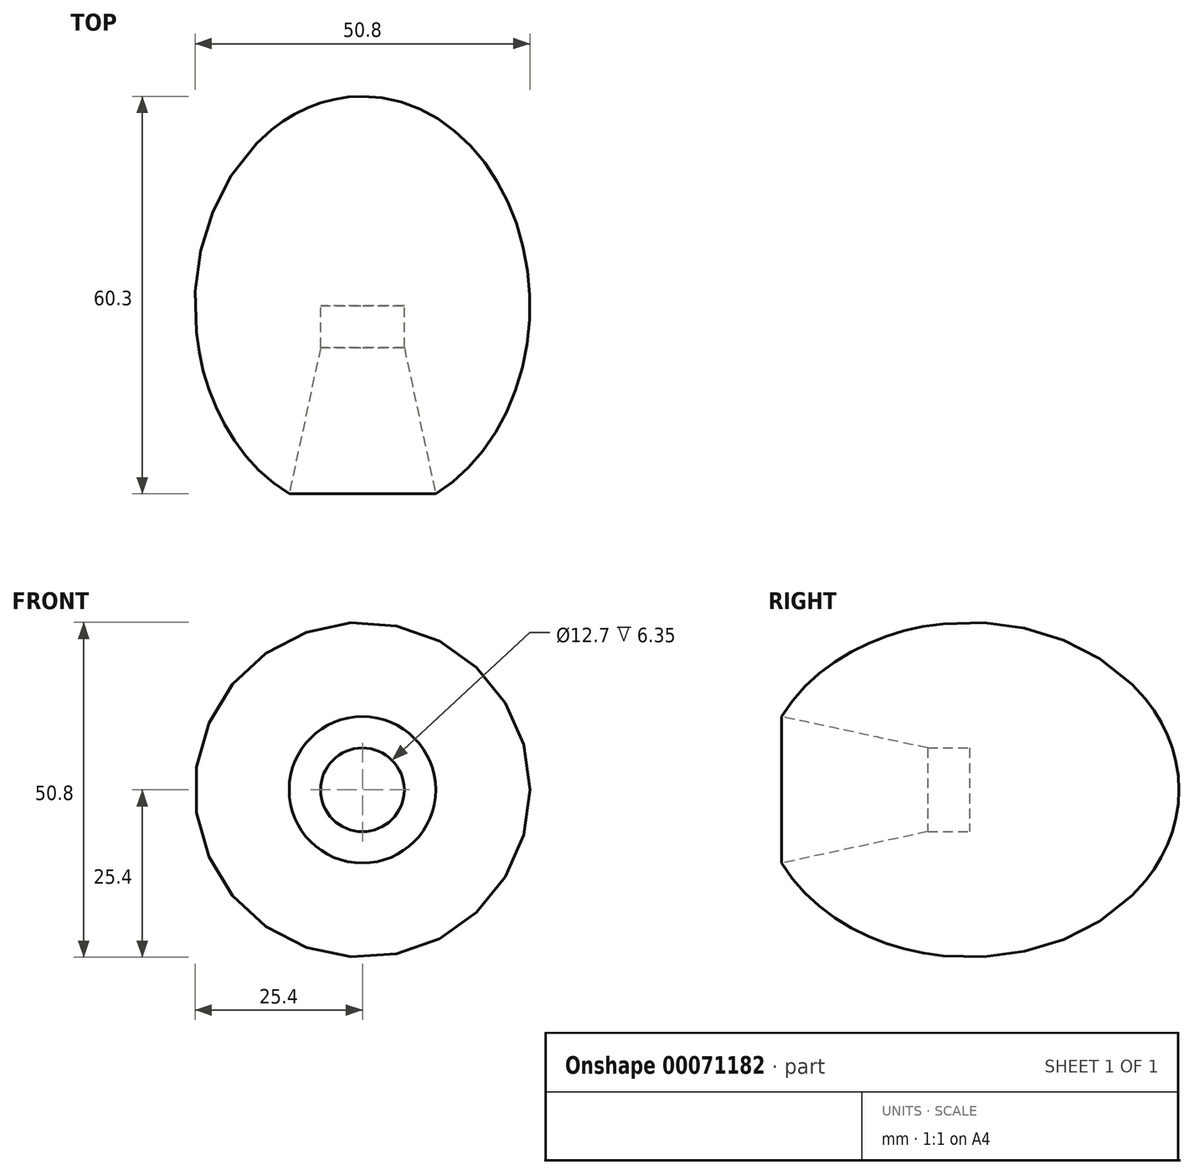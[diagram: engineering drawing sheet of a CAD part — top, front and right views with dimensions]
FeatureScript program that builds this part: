
annotation { "Feature Type Name" : "Feature", "Feature Type Description" : "" }
export const myFeature = defineFeature(function(context is Context, id is Id, definition is map)
    precondition{}
    {
        {
            var Q0;
            Q0=qCreatedBy(makeId("Top.planeOp"),FACE);
            var sketch = newSketch(context, id + "F0", { "sketchPlane" : qUnion([Q0])});
            skEllipticalArc(sketch, "E0", {});
            skLineSegment(sketch, "E1", {"start": v(0, 31.75) * mm, "end": v(0, -31.75) * mm});
            skLineSegment(sketch, "E2.bottom", {"start": v(0, 0) * mm, "end": v(6.35, 0) * mm});
            skLineSegment(sketch, "E2.left", {"start": v(0, 0) * mm, "end": v(0, -6.35) * mm});
            skLineSegment(sketch, "E2.right", {"start": v(6.35, 0) * mm, "end": v(6.35, -6.35) * mm});
            skLineSegment(sketch, "E3", {"start": v(6.35, -6.35) * mm, "end": v(11.11, -28.55) * mm});
            skPoint(sketch, "E4.end.orphan", {"position": v(0, -28.55) * mm});
            const initialGuessF0  = {"E0": [0, 0, 0, 1, 0.03175, 0.0254, 3.594409248334718, 0]};
            skSetInitialGuess(sketch, initialGuessF0);
            skSolve(sketch);
        }
        {
            var Q0;
            Q0 = qSketchRegion(id + "F0", true);
            var Q1;
            Q1=sQuery(id+"F0.wireOp",EDGE,"E1");
            revolve(context, id + "F1", {"entities" : qUnion([Q0]), "axis" : qUnion([Q1]), "revolveType" : RevolveType.FULL});
        }
    });
